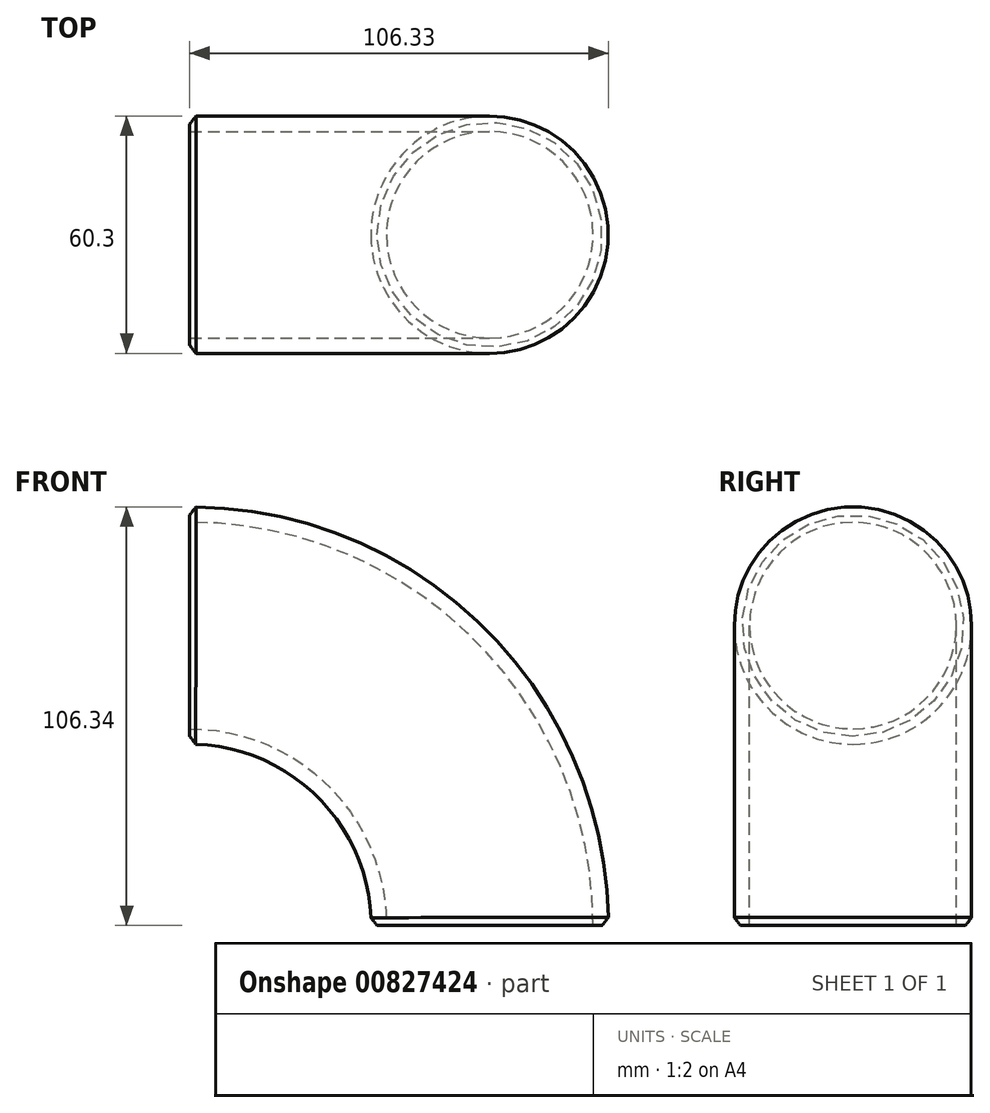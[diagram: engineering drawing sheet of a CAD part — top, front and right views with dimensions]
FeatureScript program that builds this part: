
annotation { "Feature Type Name" : "Feature", "Feature Type Description" : "" }
export const myFeature = defineFeature(function(context is Context, id is Id, definition is map)
    precondition{}
    {
        {
            var Q0;
            Q0=qCreatedBy(makeId("Right.planeOp"),FACE);
            var sketch = newSketch(context, id + "F0", { "sketchPlane" : qUnion([Q0])});
            skCircle(sketch, "E0", {"center": v(0, 76.2) * mm, "radius": 30.15 * mm});
            skCircle(sketch, "E1", {"center": v(0, 76.2) * mm, "radius": 26.25 * mm});
            skSolve(sketch);
        }
        {
            var Q0;
            Q0=qCreatedBy(makeId("Front.planeOp"),FACE);
            var sketch = newSketch(context, id + "F1", { "sketchPlane" : qUnion([Q0])});
            skArc(sketch, "E2", {"start": v(0, 76.2) * mm, "mid": v(53.88, 53.88) * mm, "end": v(76.2, 0) * mm});
            skSolve(sketch);
        }
        {
            var Q0;
            Q0=makeQuery(id+"F0.imprint","IMPRINT",FACE,{"disambiguationData":[TD([[makeQuery(id+"F0.imprint","IMPRINT",EDGE,{"derivedFrom":sQuery(id+"F0.wireOp",EDGE,"E0")}),1.0]])]});
            var Q1;
            Q1=sQuery(id+"F1.wireOp",EDGE,"E2");
            sweep(context, id + "F2", {"profiles" : qUnion([Q0]), "path" : qUnion([Q1])});
        }
        {
            var Q0;
            Q0=makeQuery(id+"F2.opSweep","CAP_EDGE",EDGE,{"disambiguationData":[OSD([sQuery(id+"F0.wireOp",EDGE,"E0"),sQuery(id+"F1.wireOp",VERTEX,"E2.start")])],"isStart":true});
            chamfer(context, id + "F3", {"entities" : qUnion([Q0]), "chamferType" : ChamferType.OFFSET_ANGLE, "width" : 1.55 * mm, "oppositeDirection" : false, "angle" : 52.5 * degree, "tangentPropagation" : true});
        }
        {
            var Q0;
            Q0=makeQuery(id+"F2.opSweep","CAP_EDGE",EDGE,{"disambiguationData":[OSD([sQuery(id+"F0.wireOp",EDGE,"E0"),sQuery(id+"F1.wireOp",VERTEX,"E2.end")])],"isStart":false});
            chamfer(context, id + "F4", {"entities" : qUnion([Q0]), "chamferType" : ChamferType.OFFSET_ANGLE, "width" : 1.55 * mm, "oppositeDirection" : false, "angle" : 52.5 * degree, "tangentPropagation" : true});
        }
    });
